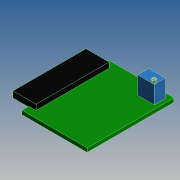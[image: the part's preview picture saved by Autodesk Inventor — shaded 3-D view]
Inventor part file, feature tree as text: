
AUTODESK INVENTOR PART (.ipt)
format: ipt  version: 2019 (Build 230136000, 136)  size: 243,200 bytes
history: native  units: mm
features: extrude x5, sketch x5
ambient origin geometry x8: Origin, YZ Plane, XZ Plane, XY Plane, X Axis, Y Axis, Z Axis, Center Point
bodies: Solid1 (feature_tree)
feature tree (10):
  extrude  "Extrusion1"  Depth=35.6mm
  extrude  "Extrusion2"  Depth=2.0mm
  extrude  "Extrusion3"  Depth=6.8mm
  extrude  "Extrusion4"  Depth=7.3mm TaperAngle=0.0deg
  extrude  "Extrusion5"  Depth=1.0mm
  sketch  "Sketch1"  dims[d0=26.8mm d1=35.6mm]
  sketch  "Sketch3"  dims[d2=1.6mm d3=0.0mm d4=2.0mm]
  sketch  "Sketch4"  dims[d5=1.5mm d6=6.8mm]
  sketch  "Sketch5"  dims[d7=4.6mm d8=7.3mm d9=0.0mm]
  sketch  "Sketch6"  dims[d10=1.7mm d11=1.0mm d12=1.0mm d13=1.0mm d14=0.0mm d15=0.5mm d16=0.5mm d17=0.0mm d18=0.3mm d19=2.5mm d20=6.5mm d21=3.0mm d22=30.0mm d23=0.0mm]
